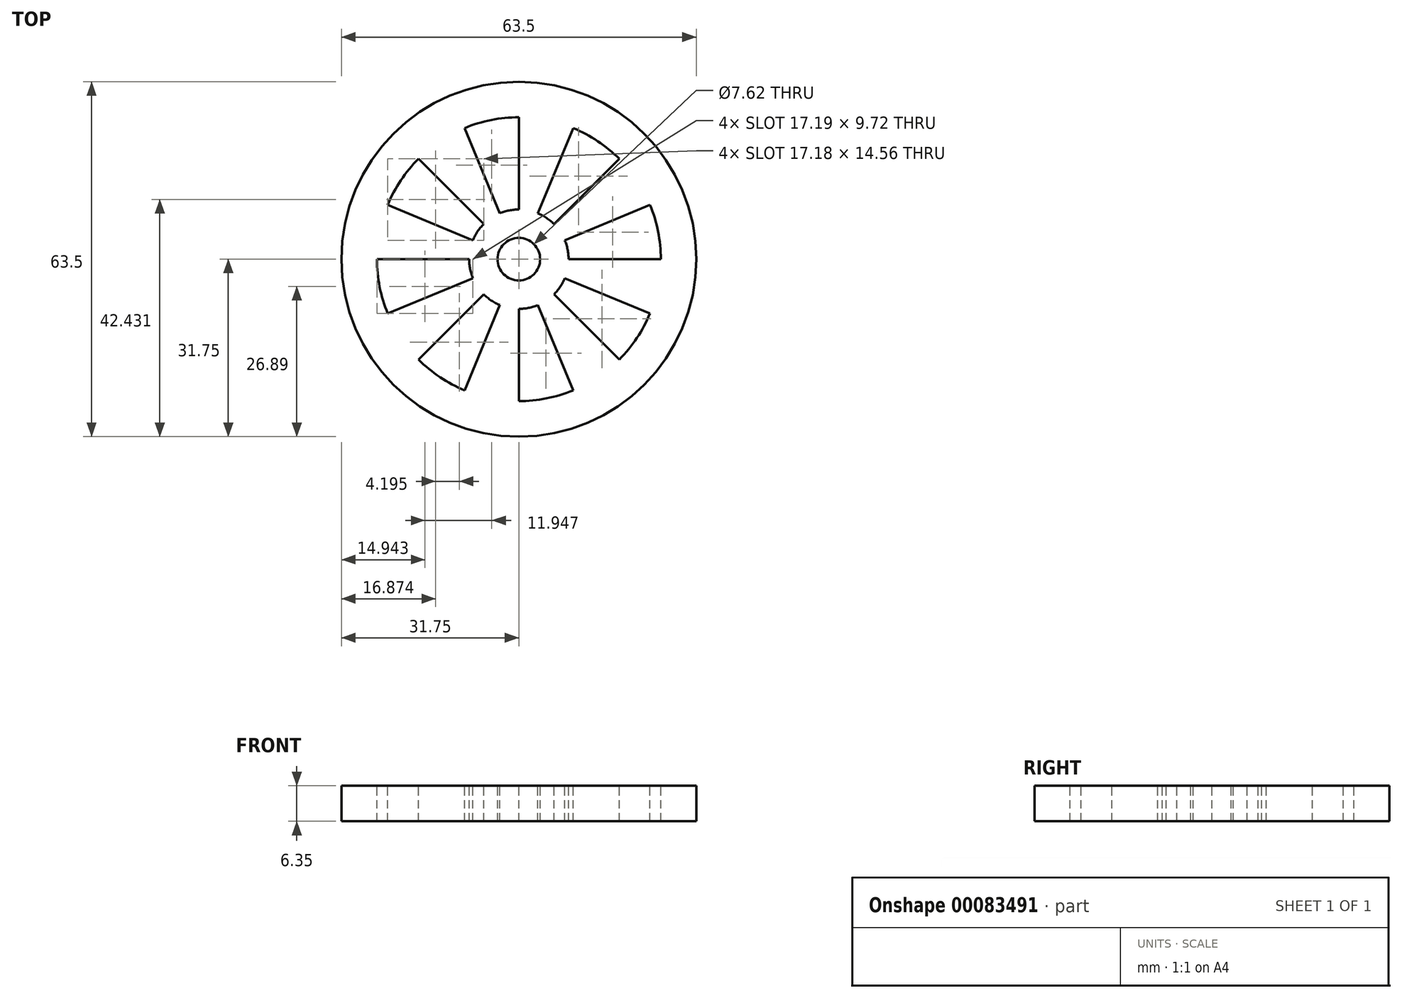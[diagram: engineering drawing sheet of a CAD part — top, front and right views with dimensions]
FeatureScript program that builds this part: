
annotation { "Feature Type Name" : "Feature", "Feature Type Description" : "" }
export const myFeature = defineFeature(function(context is Context, id is Id, definition is map)
    precondition{}
    {
        {
            var Q0;
            Q0=qCreatedBy(makeId("Top.planeOp"),FACE);
            var sketch = newSketch(context, id + "F0", { "sketchPlane" : qUnion([Q0])});
            skCircle(sketch, "E0", {"center": v(0, 0) * mm, "radius": 31.75 * mm});
            skSolve(sketch);
        }
        {
            var Q0;
            Q0 = qSketchRegion(id + "F0", true);
            extrude(context, id + "F1", {"entities" : qUnion([Q0]), "depth" : 6.35 * mm});
        }
        {
            var Q0;
            Q0=makeQuery(id+"F1.opExtrude","CAP_FACE",FACE,{"disambiguationData":[OSD([sQuery(id+"F0.wireOp",EDGE,"E0")])],"isStart":false});
            var sketch = newSketch(context, id + "F2", { "sketchPlane" : qUnion([Q0])});
            skCircle(sketch, "E1", {"center": v(0, 0) * mm, "radius": 3.81 * mm});
            skCircle(sketch, "E2", {"center": v(0, 0) * mm, "radius": 8.9 * mm});
            skLineSegment(sketch, "E3", {"start": v(0, 0) * mm, "end": v(0, 31.75) * mm});
            skLineSegment(sketch, "E4", {"start": v(0, 0) * mm, "end": v(-31.75, 0) * mm});
            skLineSegment(sketch, "E5", {"start": v(0, 0) * mm, "end": v(0, -31.75) * mm});
            skLineSegment(sketch, "E6", {"start": v(0, 0) * mm, "end": v(31.75, 0) * mm});
            skLineSegment(sketch, "E7", {"start": v(0, 0) * mm, "end": v(22.45, 22.45) * mm});
            skLineSegment(sketch, "E8", {"start": v(0, 0) * mm, "end": v(-22.45, 22.45) * mm});
            skLineSegment(sketch, "E9", {"start": v(0, 0) * mm, "end": v(-22.45, -22.45) * mm});
            skLineSegment(sketch, "E10", {"start": v(0, 0) * mm, "end": v(22.45, -22.45) * mm});
            skLineSegment(sketch, "E11", {"start": v(0, 0) * mm, "end": v(12.15, 29.33) * mm});
            skLineSegment(sketch, "E12", {"start": v(0, 0) * mm, "end": v(29.33, 12.15) * mm});
            skLineSegment(sketch, "E13", {"start": v(0, 0) * mm, "end": v(29.33, -12.15) * mm});
            skLineSegment(sketch, "E14", {"start": v(0, 0) * mm, "end": v(12.15, -29.33) * mm});
            skLineSegment(sketch, "E15", {"start": v(0, 0) * mm, "end": v(-12.15, -29.33) * mm});
            skLineSegment(sketch, "E16", {"start": v(0, 0) * mm, "end": v(-29.33, -12.15) * mm});
            skLineSegment(sketch, "E17", {"start": v(0, 0) * mm, "end": v(-29.33, 12.15) * mm});
            skLineSegment(sketch, "E18", {"start": v(0, 0) * mm, "end": v(-12.15, 29.33) * mm});
            skCircle(sketch, "E19", {"center": v(0, 0) * mm, "radius": 25.4 * mm});
            skCircle(sketch, "E20", {"center": v(0, 0) * mm, "radius": 31.75 * mm});
            skSolve(sketch);
        }
        {
            var Q0;
            {var subQ0=sQuery(id+"F2.wireOp",EDGE,"E3");var subQ1=sQuery(id+"F2.wireOp",EDGE,"E1");var subQ2=makeQuery(id+"F2.imprint","INTERSECT",VERTEX,{"derivedFrom":[subQ1,subQ0]});Q0=makeQuery(id+"F2.imprint","IMPRINT",FACE,{"disambiguationData":[TD([[makeQuery(id+"F2.imprint","IMPRINT",EDGE,{"disambiguationData":[TD([[subQ2,-1.0]])],"derivedFrom":subQ1}),1.0]])]});}
            var Q1;
            {var subQ0=sQuery(id+"F2.wireOp",EDGE,"E6");var subQ1=sQuery(id+"F2.wireOp",EDGE,"E1");var subQ2=makeQuery(id+"F2.imprint","INTERSECT",VERTEX,{"derivedFrom":[subQ1,subQ0]});Q1=makeQuery(id+"F2.imprint","IMPRINT",FACE,{"disambiguationData":[TD([[makeQuery(id+"F2.imprint","IMPRINT",EDGE,{"disambiguationData":[TD([[subQ2,1.0]])],"derivedFrom":subQ1}),1.0]])]});}
            var Q2;
            {var subQ0=sQuery(id+"F2.wireOp",EDGE,"E5");var subQ1=sQuery(id+"F2.wireOp",EDGE,"E1");var subQ2=makeQuery(id+"F2.imprint","INTERSECT",VERTEX,{"derivedFrom":[subQ1,subQ0]});Q2=makeQuery(id+"F2.imprint","IMPRINT",FACE,{"disambiguationData":[TD([[makeQuery(id+"F2.imprint","IMPRINT",EDGE,{"disambiguationData":[TD([[subQ2,-1.0]])],"derivedFrom":subQ1}),1.0]])]});}
            var Q3;
            {var subQ0=sQuery(id+"F2.wireOp",EDGE,"E4");var subQ1=sQuery(id+"F2.wireOp",EDGE,"E1");var subQ2=makeQuery(id+"F2.imprint","INTERSECT",VERTEX,{"derivedFrom":[subQ1,subQ0]});Q3=makeQuery(id+"F2.imprint","IMPRINT",FACE,{"disambiguationData":[TD([[makeQuery(id+"F2.imprint","IMPRINT",EDGE,{"disambiguationData":[TD([[subQ2,-1.0]])],"derivedFrom":subQ1}),1.0]])]});}
            var Q4;
            {var subQ0=sQuery(id+"F2.wireOp",EDGE,"E17");var subQ1=sQuery(id+"F2.wireOp",EDGE,"E1");var subQ2=makeQuery(id+"F2.imprint","INTERSECT",VERTEX,{"derivedFrom":[subQ1,subQ0]});Q4=makeQuery(id+"F2.imprint","IMPRINT",FACE,{"disambiguationData":[TD([[makeQuery(id+"F2.imprint","IMPRINT",EDGE,{"disambiguationData":[TD([[subQ2,-1.0]])],"derivedFrom":subQ1}),1.0]])]});}
            var Q5;
            {var subQ0=sQuery(id+"F2.wireOp",EDGE,"E12");var subQ1=sQuery(id+"F2.wireOp",EDGE,"E1");var subQ2=makeQuery(id+"F2.imprint","INTERSECT",VERTEX,{"derivedFrom":[subQ1,subQ0]});Q5=makeQuery(id+"F2.imprint","IMPRINT",FACE,{"disambiguationData":[TD([[makeQuery(id+"F2.imprint","IMPRINT",EDGE,{"disambiguationData":[TD([[subQ2,1.0]])],"derivedFrom":subQ1}),1.0]])]});}
            var Q6;
            {var subQ0=sQuery(id+"F2.wireOp",EDGE,"E12");var subQ1=sQuery(id+"F2.wireOp",EDGE,"E1");var subQ2=makeQuery(id+"F2.imprint","INTERSECT",VERTEX,{"derivedFrom":[subQ1,subQ0]});Q6=makeQuery(id+"F2.imprint","IMPRINT",FACE,{"disambiguationData":[TD([[makeQuery(id+"F2.imprint","IMPRINT",EDGE,{"disambiguationData":[TD([[subQ2,-1.0]])],"derivedFrom":subQ1}),1.0]])]});}
            var Q7;
            {var subQ0=sQuery(id+"F2.wireOp",EDGE,"E7");var subQ1=sQuery(id+"F2.wireOp",EDGE,"E1");var subQ2=makeQuery(id+"F2.imprint","INTERSECT",VERTEX,{"derivedFrom":[subQ1,subQ0]});Q7=makeQuery(id+"F2.imprint","IMPRINT",FACE,{"disambiguationData":[TD([[makeQuery(id+"F2.imprint","IMPRINT",EDGE,{"disambiguationData":[TD([[subQ2,-1.0]])],"derivedFrom":subQ1}),1.0]])]});}
            var Q8;
            {var subQ0=sQuery(id+"F2.wireOp",EDGE,"E11");var subQ1=sQuery(id+"F2.wireOp",EDGE,"E1");var subQ2=makeQuery(id+"F2.imprint","INTERSECT",VERTEX,{"derivedFrom":[subQ1,subQ0]});Q8=makeQuery(id+"F2.imprint","IMPRINT",FACE,{"disambiguationData":[TD([[makeQuery(id+"F2.imprint","IMPRINT",EDGE,{"disambiguationData":[TD([[subQ2,-1.0]])],"derivedFrom":subQ1}),1.0]])]});}
            var Q9;
            {var subQ0=sQuery(id+"F2.wireOp",EDGE,"E18");var subQ1=sQuery(id+"F2.wireOp",EDGE,"E1");var subQ2=makeQuery(id+"F2.imprint","INTERSECT",VERTEX,{"derivedFrom":[subQ1,subQ0]});Q9=makeQuery(id+"F2.imprint","IMPRINT",FACE,{"disambiguationData":[TD([[makeQuery(id+"F2.imprint","IMPRINT",EDGE,{"disambiguationData":[TD([[subQ2,-1.0]])],"derivedFrom":subQ1}),1.0]])]});}
            var Q10;
            {var subQ0=sQuery(id+"F2.wireOp",EDGE,"E8");var subQ1=sQuery(id+"F2.wireOp",EDGE,"E1");var subQ2=makeQuery(id+"F2.imprint","INTERSECT",VERTEX,{"derivedFrom":[subQ1,subQ0]});Q10=makeQuery(id+"F2.imprint","IMPRINT",FACE,{"disambiguationData":[TD([[makeQuery(id+"F2.imprint","IMPRINT",EDGE,{"disambiguationData":[TD([[subQ2,-1.0]])],"derivedFrom":subQ1}),1.0]])]});}
            var Q11;
            {var subQ0=sQuery(id+"F2.wireOp",EDGE,"E9");var subQ1=sQuery(id+"F2.wireOp",EDGE,"E1");var subQ2=makeQuery(id+"F2.imprint","INTERSECT",VERTEX,{"derivedFrom":[subQ1,subQ0]});Q11=makeQuery(id+"F2.imprint","IMPRINT",FACE,{"disambiguationData":[TD([[makeQuery(id+"F2.imprint","IMPRINT",EDGE,{"disambiguationData":[TD([[subQ2,-1.0]])],"derivedFrom":subQ1}),1.0]])]});}
            var Q12;
            {var subQ0=sQuery(id+"F2.wireOp",EDGE,"E16");var subQ1=sQuery(id+"F2.wireOp",EDGE,"E1");var subQ2=makeQuery(id+"F2.imprint","INTERSECT",VERTEX,{"derivedFrom":[subQ1,subQ0]});Q12=makeQuery(id+"F2.imprint","IMPRINT",FACE,{"disambiguationData":[TD([[makeQuery(id+"F2.imprint","IMPRINT",EDGE,{"disambiguationData":[TD([[subQ2,-1.0]])],"derivedFrom":subQ1}),1.0]])]});}
            var Q13;
            {var subQ0=sQuery(id+"F2.wireOp",EDGE,"E10");var subQ1=sQuery(id+"F2.wireOp",EDGE,"E1");var subQ2=makeQuery(id+"F2.imprint","INTERSECT",VERTEX,{"derivedFrom":[subQ1,subQ0]});Q13=makeQuery(id+"F2.imprint","IMPRINT",FACE,{"disambiguationData":[TD([[makeQuery(id+"F2.imprint","IMPRINT",EDGE,{"disambiguationData":[TD([[subQ2,-1.0]])],"derivedFrom":subQ1}),1.0]])]});}
            var Q14;
            {var subQ0=sQuery(id+"F2.wireOp",EDGE,"E14");var subQ1=sQuery(id+"F2.wireOp",EDGE,"E1");var subQ2=makeQuery(id+"F2.imprint","INTERSECT",VERTEX,{"derivedFrom":[subQ1,subQ0]});Q14=makeQuery(id+"F2.imprint","IMPRINT",FACE,{"disambiguationData":[TD([[makeQuery(id+"F2.imprint","IMPRINT",EDGE,{"disambiguationData":[TD([[subQ2,-1.0]])],"derivedFrom":subQ1}),1.0]])]});}
            var Q15;
            {var subQ0=sQuery(id+"F2.wireOp",EDGE,"E15");var subQ1=sQuery(id+"F2.wireOp",EDGE,"E1");var subQ2=makeQuery(id+"F2.imprint","INTERSECT",VERTEX,{"derivedFrom":[subQ1,subQ0]});Q15=makeQuery(id+"F2.imprint","IMPRINT",FACE,{"disambiguationData":[TD([[makeQuery(id+"F2.imprint","IMPRINT",EDGE,{"disambiguationData":[TD([[subQ2,-1.0]])],"derivedFrom":subQ1}),1.0]])]});}
            var Q16;
            {var subQ0=sQuery(id+"F2.wireOp",EDGE,"E3");var subQ1=sQuery(id+"F2.wireOp",EDGE,"E2");var subQ2=makeQuery(id+"F2.imprint","INTERSECT",VERTEX,{"derivedFrom":[subQ1,subQ0]});Q16=makeQuery(id+"F2.imprint","IMPRINT",FACE,{"disambiguationData":[TD([[makeQuery(id+"F2.imprint","IMPRINT",EDGE,{"disambiguationData":[TD([[subQ2,-1.0]])],"derivedFrom":subQ1}),-1.0]])]});}
            var Q17;
            {var subQ0=sQuery(id+"F2.wireOp",EDGE,"E7");var subQ1=sQuery(id+"F2.wireOp",EDGE,"E2");var subQ2=makeQuery(id+"F2.imprint","INTERSECT",VERTEX,{"derivedFrom":[subQ1,subQ0]});Q17=makeQuery(id+"F2.imprint","IMPRINT",FACE,{"disambiguationData":[TD([[makeQuery(id+"F2.imprint","IMPRINT",EDGE,{"disambiguationData":[TD([[subQ2,-1.0]])],"derivedFrom":subQ1}),-1.0]])]});}
            var Q18;
            {var subQ0=sQuery(id+"F2.wireOp",EDGE,"E12");var subQ1=sQuery(id+"F2.wireOp",EDGE,"E2");var subQ2=makeQuery(id+"F2.imprint","INTERSECT",VERTEX,{"derivedFrom":[subQ1,subQ0]});Q18=makeQuery(id+"F2.imprint","IMPRINT",FACE,{"disambiguationData":[TD([[makeQuery(id+"F2.imprint","IMPRINT",EDGE,{"disambiguationData":[TD([[subQ2,1.0]])],"derivedFrom":subQ1}),-1.0]])]});}
            var Q19;
            {var subQ0=sQuery(id+"F2.wireOp",EDGE,"E10");var subQ1=sQuery(id+"F2.wireOp",EDGE,"E2");var subQ2=makeQuery(id+"F2.imprint","INTERSECT",VERTEX,{"derivedFrom":[subQ1,subQ0]});Q19=makeQuery(id+"F2.imprint","IMPRINT",FACE,{"disambiguationData":[TD([[makeQuery(id+"F2.imprint","IMPRINT",EDGE,{"disambiguationData":[TD([[subQ2,-1.0]])],"derivedFrom":subQ1}),-1.0]])]});}
            var Q20;
            {var subQ0=sQuery(id+"F2.wireOp",EDGE,"E5");var subQ1=sQuery(id+"F2.wireOp",EDGE,"E2");var subQ2=makeQuery(id+"F2.imprint","INTERSECT",VERTEX,{"derivedFrom":[subQ1,subQ0]});Q20=makeQuery(id+"F2.imprint","IMPRINT",FACE,{"disambiguationData":[TD([[makeQuery(id+"F2.imprint","IMPRINT",EDGE,{"disambiguationData":[TD([[subQ2,-1.0]])],"derivedFrom":subQ1}),-1.0]])]});}
            var Q21;
            {var subQ0=sQuery(id+"F2.wireOp",EDGE,"E9");var subQ1=sQuery(id+"F2.wireOp",EDGE,"E2");var subQ2=makeQuery(id+"F2.imprint","INTERSECT",VERTEX,{"derivedFrom":[subQ1,subQ0]});Q21=makeQuery(id+"F2.imprint","IMPRINT",FACE,{"disambiguationData":[TD([[makeQuery(id+"F2.imprint","IMPRINT",EDGE,{"disambiguationData":[TD([[subQ2,-1.0]])],"derivedFrom":subQ1}),-1.0]])]});}
            var Q22;
            {var subQ0=sQuery(id+"F2.wireOp",EDGE,"E4");var subQ1=sQuery(id+"F2.wireOp",EDGE,"E2");var subQ2=makeQuery(id+"F2.imprint","INTERSECT",VERTEX,{"derivedFrom":[subQ1,subQ0]});Q22=makeQuery(id+"F2.imprint","IMPRINT",FACE,{"disambiguationData":[TD([[makeQuery(id+"F2.imprint","IMPRINT",EDGE,{"disambiguationData":[TD([[subQ2,-1.0]])],"derivedFrom":subQ1}),-1.0]])]});}
            var Q23;
            {var subQ0=sQuery(id+"F2.wireOp",EDGE,"E8");var subQ1=sQuery(id+"F2.wireOp",EDGE,"E2");var subQ2=makeQuery(id+"F2.imprint","INTERSECT",VERTEX,{"derivedFrom":[subQ1,subQ0]});Q23=makeQuery(id+"F2.imprint","IMPRINT",FACE,{"disambiguationData":[TD([[makeQuery(id+"F2.imprint","IMPRINT",EDGE,{"disambiguationData":[TD([[subQ2,-1.0]])],"derivedFrom":subQ1}),-1.0]])]});}
            extrude(context, id + "F3", {"entities" : qUnion([Q0, Q1, Q2, Q3, Q4, Q5, Q6, Q7, Q8, Q9, Q10, Q11, Q12, Q13, Q14, Q15, Q16, Q17, Q18, Q19, Q20, Q21, Q22, Q23]), "operationType" : NewBodyOperationType.REMOVE, "oppositeDirection" : true, "depth" : 25.4 * mm});
        }
    });
